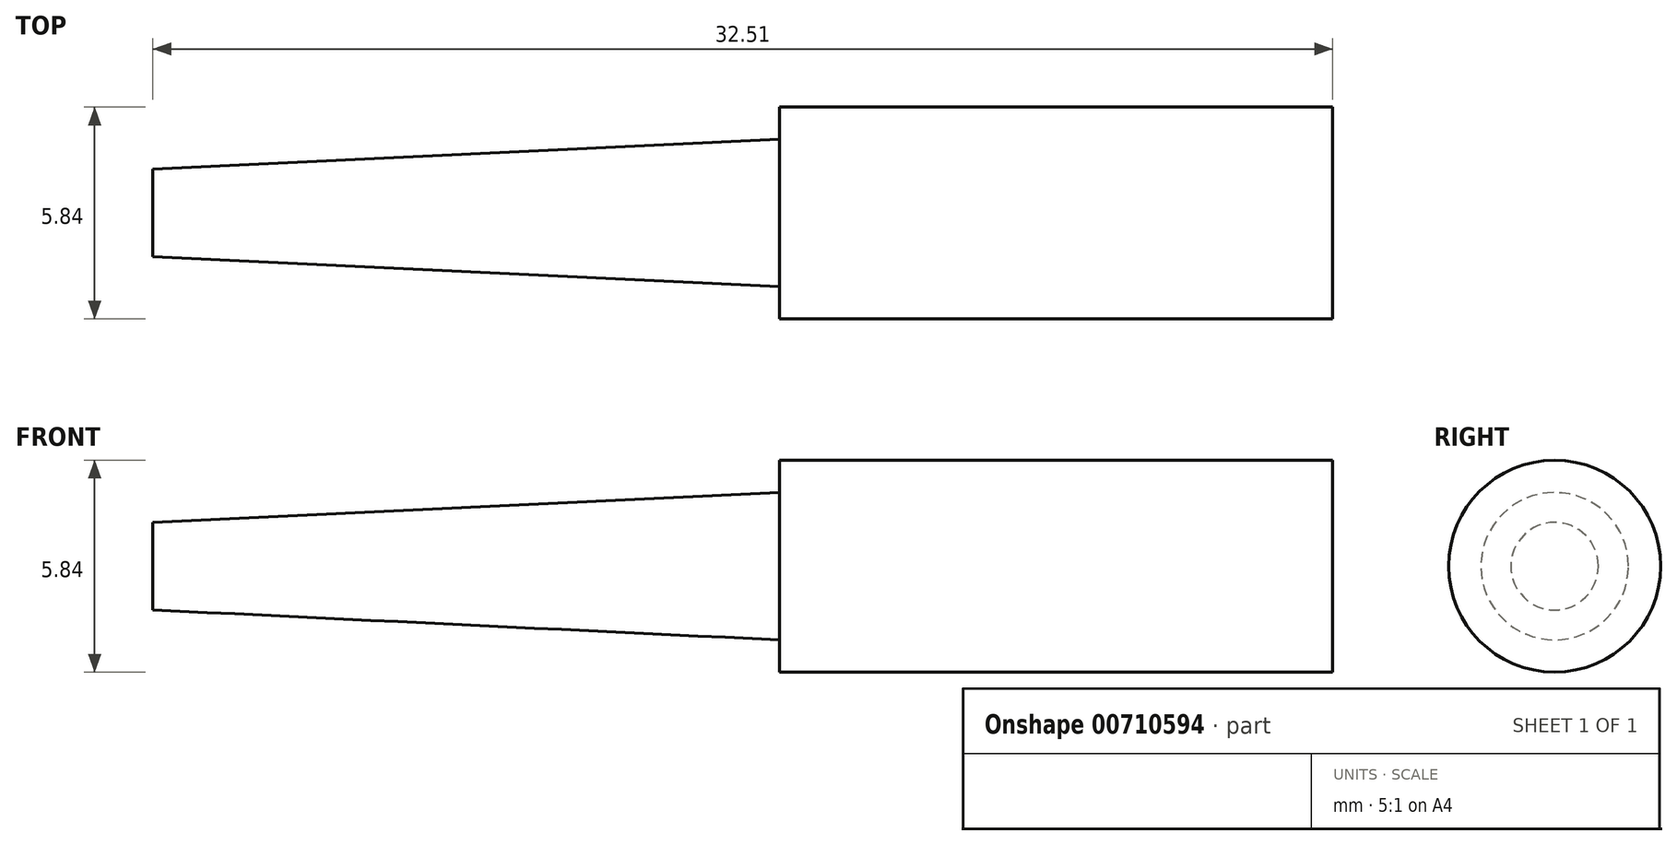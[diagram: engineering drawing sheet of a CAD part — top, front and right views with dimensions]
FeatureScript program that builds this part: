
annotation { "Feature Type Name" : "Feature", "Feature Type Description" : "" }
export const myFeature = defineFeature(function(context is Context, id is Id, definition is map)
    precondition{}
    {
        {
            var Q0;
            Q0=qCreatedBy(makeId("Front.planeOp"),FACE);
            var sketch = newSketch(context, id + "F0", { "sketchPlane" : qUnion([Q0])});
            skLineSegment(sketch, "E0", {"start": v(0, 0) * mm, "end": v(32.51, 0) * mm});
            skLineSegment(sketch, "E1", {"start": v(0, 0) * mm, "end": v(0, 1.2) * mm});
            skLineSegment(sketch, "E2", {"start": v(0, 1.2) * mm, "end": v(17.27, 2.03) * mm});
            skLineSegment(sketch, "E3", {"start": v(17.27, 2.03) * mm, "end": v(17.27, 2.92) * mm});
            skLineSegment(sketch, "E4", {"start": v(17.27, 2.92) * mm, "end": v(32.51, 2.92) * mm});
            skLineSegment(sketch, "E5", {"start": v(32.51, 2.92) * mm, "end": v(32.51, 0) * mm});
            skLineSegment(sketch, "E6", {"start": v(0, 0) * mm, "end": v(-22.64, 0) * mm, "construction": true});
            skSolve(sketch);
        }
        {
            var Q0;
            Q0 = qSketchRegion(id + "F0", true);
            var Q1;
            Q1=sQuery(id+"F0.wireOp",EDGE,"E6");
            revolve(context, id + "F1", {"surfaceOperationType" : NewSurfaceOperationType.NEW, "entities" : qUnion([Q0]), "axis" : qUnion([Q1]), "revolveType" : RevolveType.FULL});
        }
    });
